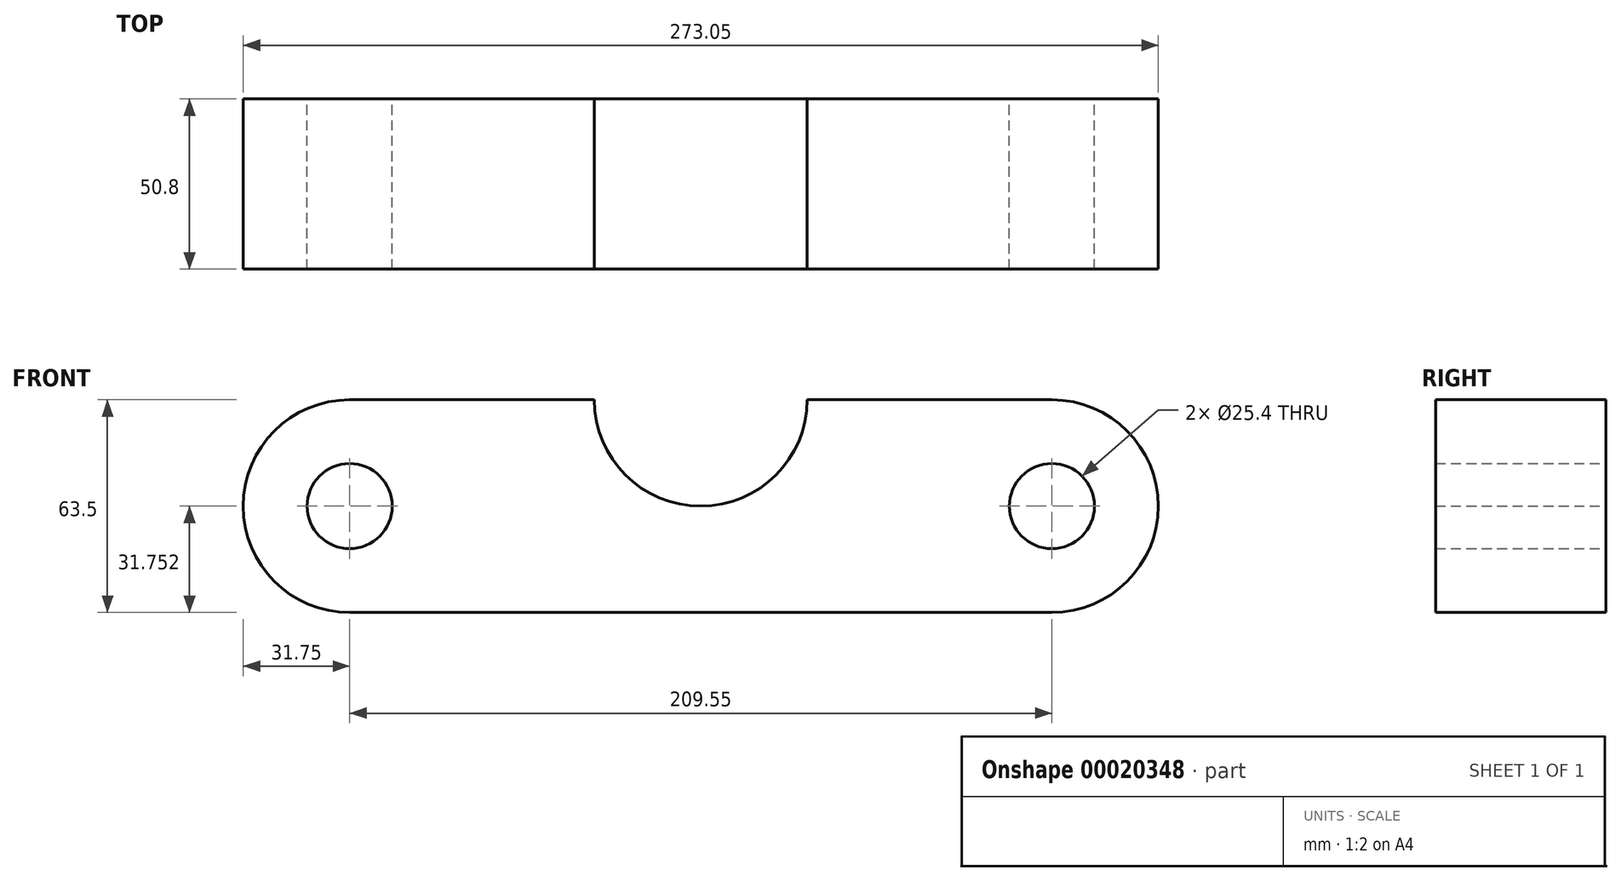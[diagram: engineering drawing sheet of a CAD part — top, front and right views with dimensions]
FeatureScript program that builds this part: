
annotation { "Feature Type Name" : "Feature", "Feature Type Description" : "" }
export const myFeature = defineFeature(function(context is Context, id is Id, definition is map)
    precondition{}
    {
        {
            var Q0;
            Q0=qCreatedBy(makeId("Front.planeOp"),FACE);
            var sketch = newSketch(context, id + "F0", { "sketchPlane" : qUnion([Q0])});
            skLineSegment(sketch, "E0.bottom", {"start": v(-59.07, 35.54) * mm, "end": v(13.96, 35.54) * mm});
            skLineSegment(sketch, "E0.top", {"start": v(-59.07, -27.96) * mm, "end": v(45.7, -27.96) * mm});
            skLineSegment(sketch, "E0.left", {"start": v(-59.07, 35.54) * mm, "end": v(-59.07, -27.96) * mm});
            skLineSegment(sketch, "E0.right", {"start": v(45.7, 3.8) * mm, "end": v(45.7, -27.96) * mm});
            skArc(sketch, "E1", {"start": v(-59.07, 35.54) * mm, "mid": v(-90.82, 3.8) * mm, "end": v(-59.07, -27.96) * mm});
            skCircle(sketch, "E2", {"center": v(-59.07, 3.8) * mm, "radius": 12.7 * mm});
            skArc(sketch, "E3", {"start": v(13.96, 35.54) * mm, "mid": v(23.25, 13.1) * mm, "end": v(45.7, 3.8) * mm});
            skSolve(sketch);
        }
        {
            var Q0;
            {var subQ6=sQuery(id+"F0.wireOp",EDGE,"E0.bottom");Q0=makeQuery(id+"F0.imprint","IMPRINT",FACE,{"disambiguationData":[TD([[makeQuery(id+"F0.imprint","IMPRINT",EDGE,{"derivedFrom":subQ6}),-1.0]])]});}
            var Q1;
            {var subQ4=sQuery(id+"F0.wireOp",EDGE,"E1");Q1=makeQuery(id+"F0.imprint","IMPRINT",FACE,{"disambiguationData":[TD([[makeQuery(id+"F0.imprint","IMPRINT",EDGE,{"derivedFrom":subQ4}),1.0]])]});}
            extrude(context, id + "F1", {"entities" : qUnion([Q0, Q1]), "depth" : 50.8 * mm});
        }
        {
            var Q0;
            Q0=makeQuery(id+"F1.opExtrude","SWEPT_BODY",BODY,{"disambiguationData":[OSD([sQuery(id+"F0.wireOp",EDGE,"E0.bottom"),sQuery(id+"F0.wireOp",EDGE,"E0.top"),sQuery(id+"F0.wireOp",EDGE,"E0.right"),sQuery(id+"F0.wireOp",EDGE,"E1"),sQuery(id+"F0.wireOp",EDGE,"E2"),sQuery(id+"F0.wireOp",EDGE,"E3")])]});
            var Q1;
            Q1=makeQuery(id+"F1.opExtrude","SWEPT_FACE",FACE,{"disambiguationData":[OSD([sQuery(id+"F0.wireOp",EDGE,"E0.right")])]});
            mirror(context, id + "F2", {"operationType" : NewBodyOperationType.ADD, "entities" : qUnion([Q0]), "mirrorPlane" : qUnion([Q1])});
        }
    });
